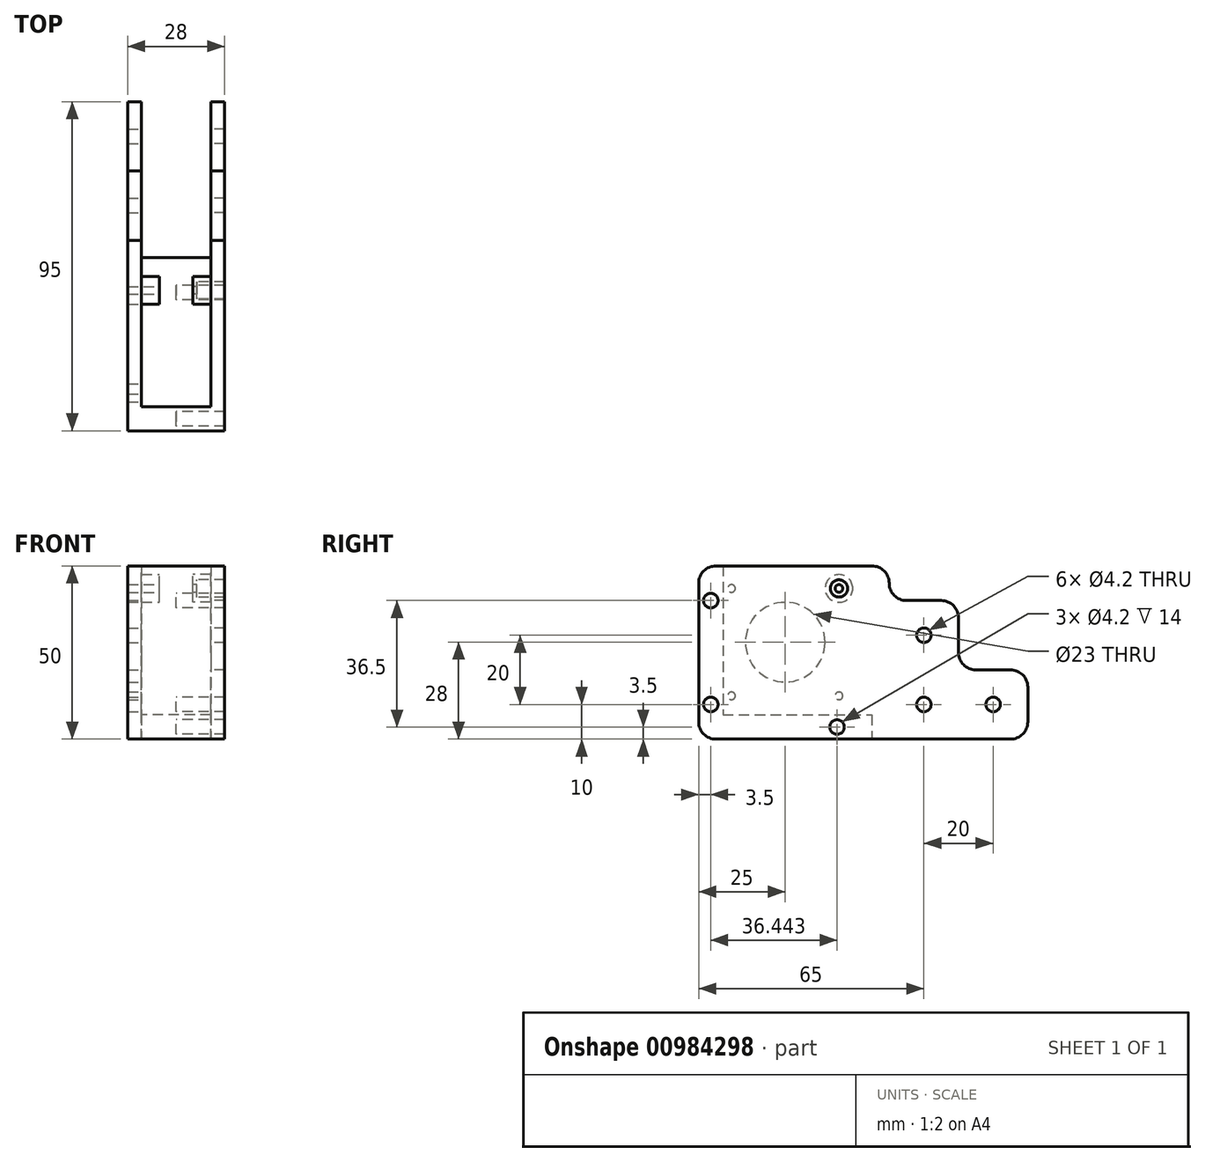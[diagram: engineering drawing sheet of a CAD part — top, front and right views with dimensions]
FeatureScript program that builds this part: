
annotation { "Feature Type Name" : "Feature", "Feature Type Description" : "" }
export const myFeature = defineFeature(function(context is Context, id is Id, definition is map)
    precondition{}
    {
        {
            var Q0;
            Q0=qCreatedBy(makeId("Right.planeOp"),FACE);
            var sketch = newSketch(context, id + "F0", { "sketchPlane" : qUnion([Q0])});
            skLineSegment(sketch, "E0", {"start": v(-47.5, 20) * mm, "end": v(-47.5, -20) * mm});
            skLineSegment(sketch, "E1", {"start": v(-42.5, -25) * mm, "end": v(42.5, -25) * mm});
            skLineSegment(sketch, "E2", {"start": v(47.5, -20) * mm, "end": v(47.5, -10) * mm});
            skLineSegment(sketch, "E3", {"start": v(42.5, -5) * mm, "end": v(32.5, -5) * mm});
            skLineSegment(sketch, "E4", {"start": v(27.5, 0) * mm, "end": v(27.5, 10) * mm});
            skLineSegment(sketch, "E5", {"start": v(22.5, 15) * mm, "end": v(12.5, 15) * mm});
            skLineSegment(sketch, "E6", {"start": v(7.5, 20) * mm, "end": v(7.5, 20) * mm});
            skLineSegment(sketch, "E7", {"start": v(2.5, 25) * mm, "end": v(-42.5, 25) * mm});
            skCircle(sketch, "E8", {"center": v(17.5, 5) * mm, "radius": 2.1 * mm});
            skCircle(sketch, "E9", {"center": v(17.5, -15) * mm, "radius": 2.1 * mm});
            skCircle(sketch, "E10", {"center": v(37.5, -15) * mm, "radius": 2.1 * mm});
            skCircle(sketch, "E11", {"center": v(-22.5, 3) * mm, "radius": 11.5 * mm});
            skCircle(sketch, "E12", {"center": v(-38, 18.5) * mm, "radius": 1.1 * mm});
            skCircle(sketch, "E13", {"center": v(-38, -12.5) * mm, "radius": 1.1 * mm});
            skCircle(sketch, "E14", {"center": v(-7, 18.5) * mm, "radius": 1.1 * mm});
            skCircle(sketch, "E15", {"center": v(-7, -12.5) * mm, "radius": 1.1 * mm});
            skPoint(sketch, "E16.visualSharp", {"position": v(-47.5, 25) * mm});
            skArc(sketch, "E16.filletArc", {"start": v(-42.5, 25) * mm, "mid": v(-46.04, 23.54) * mm, "end": v(-47.5, 20) * mm});
            skPoint(sketch, "E17.visualSharp", {"position": v(-47.5, -25) * mm});
            skArc(sketch, "E17.filletArc", {"start": v(-47.5, -20) * mm, "mid": v(-46.04, -23.54) * mm, "end": v(-42.5, -25) * mm});
            skPoint(sketch, "E18.visualSharp", {"position": v(47.5, -25) * mm});
            skArc(sketch, "E18.filletArc", {"start": v(42.5, -25) * mm, "mid": v(46.04, -23.54) * mm, "end": v(47.5, -20) * mm});
            skPoint(sketch, "E19.visualSharp", {"position": v(47.5, -5) * mm});
            skArc(sketch, "E19.filletArc", {"start": v(47.5, -10) * mm, "mid": v(46.04, -6.46) * mm, "end": v(42.5, -5) * mm});
            skPoint(sketch, "E20.visualSharp", {"position": v(27.5, -5) * mm});
            skArc(sketch, "E20.filletArc", {"start": v(27.5, 0) * mm, "mid": v(28.96, -3.54) * mm, "end": v(32.5, -5) * mm});
            skPoint(sketch, "E21.visualSharp", {"position": v(27.5, 15) * mm});
            skArc(sketch, "E21.filletArc", {"start": v(27.5, 10) * mm, "mid": v(26.04, 13.54) * mm, "end": v(22.5, 15) * mm});
            skPoint(sketch, "E22.visualSharp", {"position": v(7.5, 25) * mm});
            skArc(sketch, "E22.filletArc", {"start": v(7.5, 20) * mm, "mid": v(6.04, 23.54) * mm, "end": v(2.5, 25) * mm});
            skPoint(sketch, "E23.visualSharp", {"position": v(7.5, 15) * mm});
            skArc(sketch, "E23.filletArc", {"start": v(7.5, 20) * mm, "mid": v(8.96, 16.46) * mm, "end": v(12.5, 15) * mm});
            skCircle(sketch, "E24", {"center": v(-44, -15) * mm, "radius": 2.1 * mm});
            skCircle(sketch, "E25", {"center": v(-44, 15) * mm, "radius": 2.1 * mm});
            skCircle(sketch, "E26", {"center": v(-7.56, -21.5) * mm, "radius": 2.1 * mm});
            skLineSegment(sketch, "E27", {"start": v(-40.5, 25) * mm, "end": v(-40.5, -18) * mm});
            skLineSegment(sketch, "E28", {"start": v(-40.5, -18) * mm, "end": v(2.44, -18) * mm});
            skLineSegment(sketch, "E29", {"start": v(2.44, -18) * mm, "end": v(2.44, -25) * mm});
            skCircle(sketch, "E30", {"center": v(-7, 18.5) * mm, "radius": 2.5 * mm});
            skCircle(sketch, "E31", {"center": v(-7, 18.5) * mm, "radius": 4 * mm});
            skSolve(sketch);
        }
        {
            var Q0;
            Q0=makeQuery(id+"F0.imprint","IMPRINT",FACE,{"disambiguationData":[TD([[makeQuery(id+"F0.imprint","IMPRINT",EDGE,{"derivedFrom":sQuery(id+"F0.wireOp",EDGE,"E0")}),1.0]])]});
            var Q1;
            Q1=makeQuery(id+"F0.imprint","IMPRINT",FACE,{"disambiguationData":[TD([[makeQuery(id+"F0.imprint","IMPRINT",EDGE,{"derivedFrom":sQuery(id+"F0.wireOp",EDGE,"E2")}),1.0]])]});
            var Q2;
            Q2=makeQuery(id+"F0.imprint","IMPRINT",FACE,{"disambiguationData":[TD([[makeQuery(id+"F0.imprint","IMPRINT",EDGE,{"derivedFrom":sQuery(id+"F0.wireOp",EDGE,"E25")}),1.0]])]});
            var Q3;
            Q3=makeQuery(id+"F0.imprint","IMPRINT",FACE,{"disambiguationData":[TD([[makeQuery(id+"F0.imprint","IMPRINT",EDGE,{"derivedFrom":sQuery(id+"F0.wireOp",EDGE,"E24")}),1.0]])]});
            var Q4;
            Q4=makeQuery(id+"F0.imprint","IMPRINT",FACE,{"disambiguationData":[TD([[makeQuery(id+"F0.imprint","IMPRINT",EDGE,{"derivedFrom":sQuery(id+"F0.wireOp",EDGE,"E26")}),1.0]])]});
            var Q5;
            Q5=makeQuery(id+"F0.imprint","IMPRINT",FACE,{"disambiguationData":[TD([[makeQuery(id+"F0.imprint","IMPRINT",EDGE,{"derivedFrom":sQuery(id+"F0.wireOp",EDGE,"E30")}),-1.0]])]});
            var Q6;
            Q6=makeQuery(id+"F0.imprint","IMPRINT",FACE,{"disambiguationData":[TD([[makeQuery(id+"F0.imprint","IMPRINT",EDGE,{"derivedFrom":sQuery(id+"F0.wireOp",EDGE,"E14")}),-1.0]])]});
            extrude(context, id + "F1", {"entities" : qUnion([Q0, Q1, Q2, Q3, Q4, Q5, Q6]), "oppositeDirection" : true, "depth" : 14 * mm, "offsetDistance" : 25 * mm, "hasSecondDirection" : true, "secondDirectionOppositeDirection" : true, "secondDirectionDepth" : 10 * mm});
        }
        {
            var Q0;
            Q0=makeQuery(id+"F0.imprint","IMPRINT",FACE,{"disambiguationData":[TD([[makeQuery(id+"F0.imprint","IMPRINT",EDGE,{"derivedFrom":sQuery(id+"F0.wireOp",EDGE,"E0")}),1.0]])]});
            var Q1;
            Q1=makeQuery(id+"F0.imprint","IMPRINT",FACE,{"disambiguationData":[TD([[makeQuery(id+"F0.imprint","IMPRINT",EDGE,{"derivedFrom":sQuery(id+"F0.wireOp",EDGE,"E12")}),1.0]])]});
            var Q2;
            Q2=makeQuery(id+"F0.imprint","IMPRINT",FACE,{"disambiguationData":[TD([[makeQuery(id+"F0.imprint","IMPRINT",EDGE,{"derivedFrom":sQuery(id+"F0.wireOp",EDGE,"E13")}),1.0]])]});
            var Q3;
            Q3=makeQuery(id+"F0.imprint","IMPRINT",FACE,{"disambiguationData":[TD([[makeQuery(id+"F0.imprint","IMPRINT",EDGE,{"derivedFrom":sQuery(id+"F0.wireOp",EDGE,"E15")}),1.0]])]});
            var Q4;
            Q4=makeQuery(id+"F0.imprint","IMPRINT",FACE,{"disambiguationData":[TD([[makeQuery(id+"F0.imprint","IMPRINT",EDGE,{"derivedFrom":sQuery(id+"F0.wireOp",EDGE,"E2")}),1.0]])]});
            var Q5;
            Q5=makeQuery(id+"F0.imprint","IMPRINT",FACE,{"disambiguationData":[TD([[makeQuery(id+"F0.imprint","IMPRINT",EDGE,{"derivedFrom":sQuery(id+"F0.wireOp",EDGE,"E30")}),-1.0]])]});
            var Q6;
            Q6=makeQuery(id+"F0.imprint","IMPRINT",FACE,{"disambiguationData":[TD([[makeQuery(id+"F0.imprint","IMPRINT",EDGE,{"derivedFrom":sQuery(id+"F0.wireOp",EDGE,"E11")}),1.0]])]});
            extrude(context, id + "F2", {"entities" : qUnion([Q0, Q1, Q2, Q3, Q4, Q5, Q6]), "operationType" : NewBodyOperationType.ADD, "depth" : 14 * mm, "offsetDistance" : 25 * mm, "hasSecondDirection" : true, "secondDirectionOppositeDirection" : false, "secondDirectionDepth" : 10 * mm});
        }
        {
            var Q0;
            Q0=makeQuery(id+"F0.imprint","IMPRINT",FACE,{"disambiguationData":[TD([[makeQuery(id+"F0.imprint","IMPRINT",EDGE,{"derivedFrom":sQuery(id+"F0.wireOp",EDGE,"E0")}),1.0]])]});
            var Q1;
            Q1=makeQuery(id+"F0.imprint","IMPRINT",FACE,{"disambiguationData":[TD([[makeQuery(id+"F0.imprint","IMPRINT",EDGE,{"derivedFrom":sQuery(id+"F0.wireOp",EDGE,"E25")}),1.0]])]});
            var Q2;
            Q2=makeQuery(id+"F0.imprint","IMPRINT",FACE,{"disambiguationData":[TD([[makeQuery(id+"F0.imprint","IMPRINT",EDGE,{"derivedFrom":sQuery(id+"F0.wireOp",EDGE,"E24")}),1.0]])]});
            var Q3;
            Q3=makeQuery(id+"F0.imprint","IMPRINT",FACE,{"disambiguationData":[TD([[makeQuery(id+"F0.imprint","IMPRINT",EDGE,{"derivedFrom":sQuery(id+"F0.wireOp",EDGE,"E26")}),1.0]])]});
            extrude(context, id + "F3", {"entities" : qUnion([Q0, Q1, Q2, Q3]), "operationType" : NewBodyOperationType.ADD, "depth" : 10 * mm, "offsetDistance" : 25 * mm, "hasSecondDirection" : true, "secondDirectionOppositeDirection" : true, "secondDirectionDepth" : 10 * mm});
        }
        {
            var Q0;
            Q0=makeQuery(id+"F0.imprint","IMPRINT",FACE,{"disambiguationData":[TD([[makeQuery(id+"F0.imprint","IMPRINT",EDGE,{"derivedFrom":sQuery(id+"F0.wireOp",EDGE,"E24")}),1.0]])]});
            var Q1;
            Q1=makeQuery(id+"F0.imprint","IMPRINT",FACE,{"disambiguationData":[TD([[makeQuery(id+"F0.imprint","IMPRINT",EDGE,{"derivedFrom":sQuery(id+"F0.wireOp",EDGE,"E25")}),1.0]])]});
            var Q2;
            Q2=makeQuery(id+"F0.imprint","IMPRINT",FACE,{"disambiguationData":[TD([[makeQuery(id+"F0.imprint","IMPRINT",EDGE,{"derivedFrom":sQuery(id+"F0.wireOp",EDGE,"E26")}),1.0]])]});
            extrude(context, id + "F4", {"entities" : qUnion([Q0, Q1, Q2]), "operationType" : NewBodyOperationType.REMOVE, "endBound" : BoundingType.THROUGH_ALL, "depth" : 10 * mm, "offsetDistance" : 25 * mm});
        }
        {
            var Q0;
            Q0=makeQuery(id+"F0.imprint","IMPRINT",FACE,{"disambiguationData":[TD([[makeQuery(id+"F0.imprint","IMPRINT",EDGE,{"derivedFrom":sQuery(id+"F0.wireOp",EDGE,"E30")}),-1.0]])]});
            extrude(context, id + "F5", {"entities" : qUnion([Q0]), "operationType" : NewBodyOperationType.ADD, "depth" : 10 * mm, "offsetDistance" : 25 * mm, "hasSecondDirection" : true, "secondDirectionOppositeDirection" : false, "secondDirectionDepth" : 4.8 * mm});
        }
        {
            var Q0;
            Q0=makeQuery(id+"F0.imprint","IMPRINT",FACE,{"disambiguationData":[TD([[makeQuery(id+"F0.imprint","IMPRINT",EDGE,{"derivedFrom":sQuery(id+"F0.wireOp",EDGE,"E14")}),-1.0]])]});
            extrude(context, id + "F6", {"entities" : qUnion([Q0]), "operationType" : NewBodyOperationType.ADD, "depth" : 6 * mm, "offsetDistance" : 25 * mm, "hasSecondDirection" : true, "secondDirectionOppositeDirection" : false, "secondDirectionDepth" : 4.8 * mm});
        }
        {
            var Q0;
            Q0=makeQuery(id+"F0.imprint","IMPRINT",FACE,{"disambiguationData":[TD([[makeQuery(id+"F0.imprint","IMPRINT",EDGE,{"derivedFrom":sQuery(id+"F0.wireOp",EDGE,"E30")}),-1.0]])]});
            var Q1;
            Q1=makeQuery(id+"F0.imprint","IMPRINT",FACE,{"disambiguationData":[TD([[makeQuery(id+"F0.imprint","IMPRINT",EDGE,{"derivedFrom":sQuery(id+"F0.wireOp",EDGE,"E14")}),-1.0]])]});
            extrude(context, id + "F7", {"entities" : qUnion([Q0, Q1]), "operationType" : NewBodyOperationType.ADD, "oppositeDirection" : true, "depth" : 10 * mm, "offsetDistance" : 25 * mm, "hasSecondDirection" : true, "secondDirectionOppositeDirection" : true, "secondDirectionDepth" : 4.8 * mm});
        }
    });
